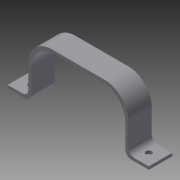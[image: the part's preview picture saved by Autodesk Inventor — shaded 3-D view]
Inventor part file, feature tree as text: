
AUTODESK INVENTOR PART (.ipt)
format: ipt  version: 2015 (Build 190159000, 159)  size: 139,264 bytes
history: native  units: in
note: dims shown in document units (in); Inventor stores cm internally (conversion verified against a paired STEP export)
features: sketch x2, projected_geometry x2, extrude x1, hole x1, fillet x1
ambient origin geometry x8: Origin, YZ Plane, XZ Plane, XY Plane, X Axis, Y Axis, Z Axis, Center Point
bodies: Solid1 (feature_tree)
feature tree (7):
  extrude  "Extrusion1"  Depth=4.0in
  hole  "Hole1"  [1 undecoded]
  fillet  "Fillet1"  Radius=1.125in
  sketch  "Sketch1"  dims[d0=4.0in d1=1.5in]
  sketch  "Sketch2"  dims[d2=1.0in d3=1.0in d4=1.125in d5=0.125in d6=0.125in d7=0.5in d8=0.25in d9=0.25in d10=0.25in d11=1.0in d12=0.0in d13=0.5in d14=0.5in d15=0.5in d16=0.5in d17=0.25in d18=0.75in d19=0.375in d20=0.25in d21=0.5635in d22=1.0in d23=0.8108in d24=0.125in]
  projected_geometry  "Projected Loop1"
  projected_geometry  "Projected Loop2"
note: 1 required parameter value undecoded (feature->parameter linkage not recoverable at this tier; creation-order binding heuristic only, values carry confidence <= 0.55)
